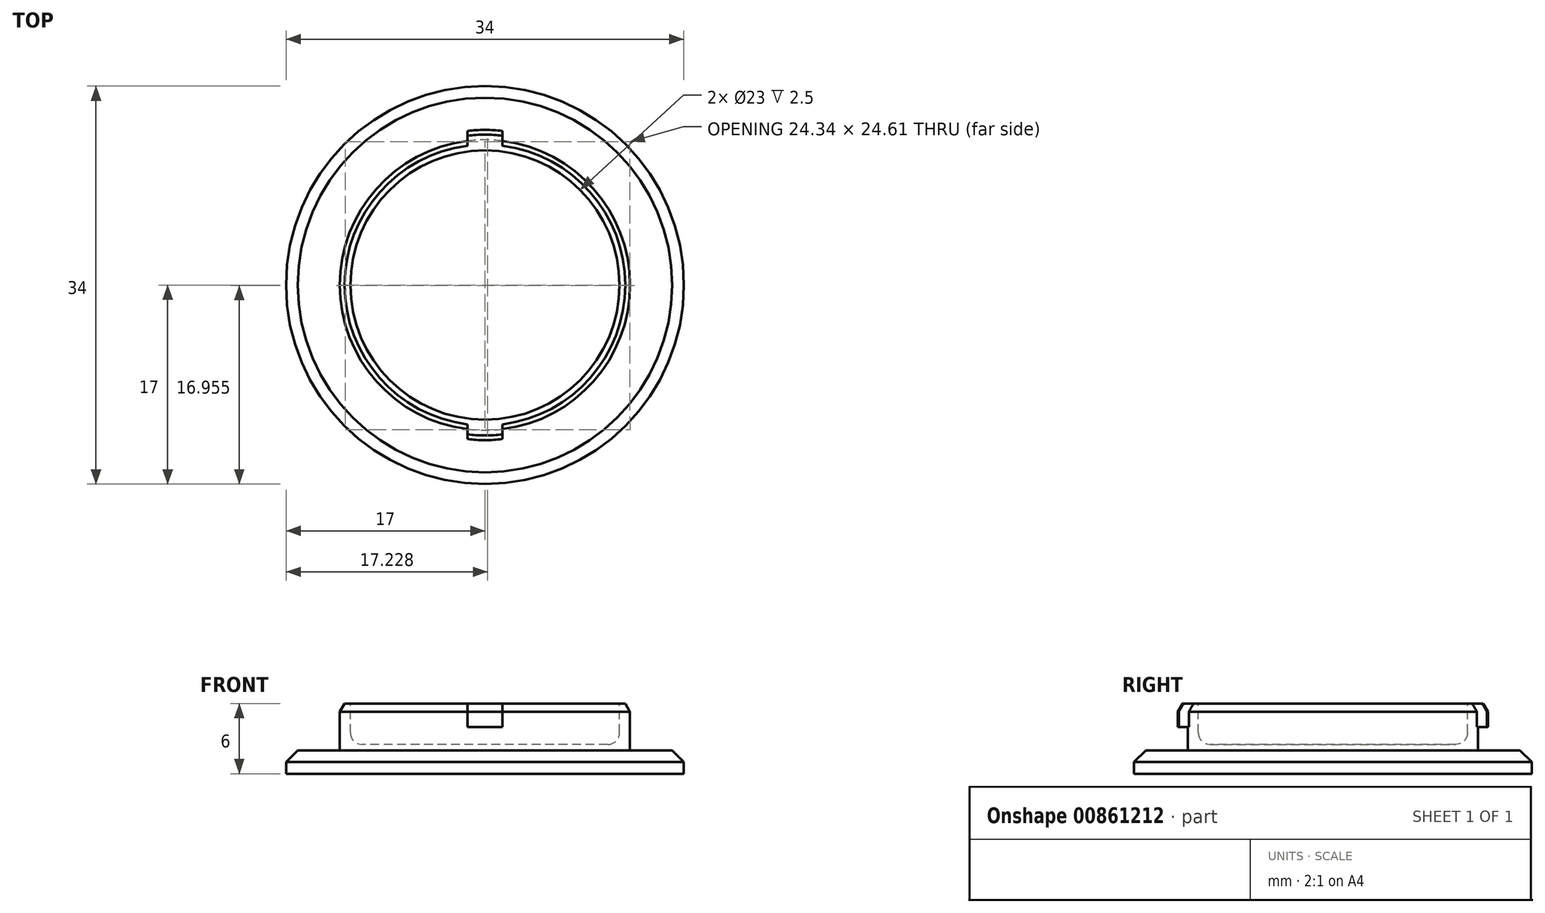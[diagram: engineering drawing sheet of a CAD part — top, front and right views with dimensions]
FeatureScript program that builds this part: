
annotation { "Feature Type Name" : "Feature", "Feature Type Description" : "" }
export const myFeature = defineFeature(function(context is Context, id is Id, definition is map)
    precondition{}
    {
        {
            var Q0;
            Q0=qCreatedBy(makeId("Top.planeOp"),FACE);
            var sketch = newSketch(context, id + "F0", { "sketchPlane" : qUnion([Q0])});
            skCircle(sketch, "E0", {"center": v(0, 0) * mm, "radius": 17 * mm});
            skSolve(sketch);
        }
        {
            var Q0;
            Q0=makeQuery(id+"F0.imprint","IMPRINT",FACE,{"disambiguationData":[TD([[makeQuery(id+"F0.imprint","IMPRINT",EDGE,{"derivedFrom":sQuery(id+"F0.wireOp",EDGE,"E0")}),1.0]])]});
            extrude(context, id + "F1", {"entities" : qUnion([Q0]), "depth" : 2 * mm, "offsetDistance" : 25 * mm});
        }
        {
            var Q0;
            Q0=makeQuery(id+"F1.opExtrude","CAP_FACE",FACE,{"disambiguationData":[OSD([sQuery(id+"F0.wireOp",EDGE,"E0")])],"isStart":false});
            var sketch = newSketch(context, id + "F2", { "sketchPlane" : qUnion([Q0])});
            skCircle(sketch, "E1", {"center": v(0, 0) * mm, "radius": 12.4 * mm});
            skSolve(sketch);
        }
        {
            var Q0;
            Q0=makeQuery(id+"F2.imprint","IMPRINT",FACE,{"disambiguationData":[TD([[makeQuery(id+"F2.imprint","IMPRINT",EDGE,{"derivedFrom":sQuery(id+"F2.wireOp",EDGE,"E1")}),1.0]])]});
            extrude(context, id + "F3", {"entities" : qUnion([Q0]), "operationType" : NewBodyOperationType.ADD, "depth" : 4 * mm, "offsetDistance" : 25 * mm});
        }
        {
            var Q0;
            Q0=makeQuery(id+"F3.opExtrude","CAP_FACE",FACE,{"disambiguationData":[OSD([sQuery(id+"F2.wireOp",EDGE,"E1")])],"isStart":false});
            var sketch = newSketch(context, id + "F4", { "sketchPlane" : qUnion([Q0])});
            skCircle(sketch, "E2", {"center": v(0, 0) * mm, "radius": 11.5 * mm});
            skSolve(sketch);
        }
        {
            var Q0;
            Q0=makeQuery(id+"F4.imprint","IMPRINT",FACE,{"disambiguationData":[TD([[makeQuery(id+"F4.imprint","IMPRINT",EDGE,{"derivedFrom":sQuery(id+"F4.wireOp",EDGE,"E2")}),1.0]])]});
            extrude(context, id + "F5", {"entities" : qUnion([Q0]), "operationType" : NewBodyOperationType.REMOVE, "oppositeDirection" : true, "depth" : 3.5 * mm, "offsetDistance" : 25 * mm});
        }
        {
            var Q0;
            Q0=makeQuery(id+"F3.opExtrude","CAP_FACE",FACE,{"disambiguationData":[OSD([sQuery(id+"F2.wireOp",EDGE,"E1")])],"isStart":false});
            var sketch = newSketch(context, id + "F6", { "sketchPlane" : qUnion([Q0])});
            skArc(sketch, "E3", {"start": v(-1.5, -13.16) * mm, "mid": v(0, -13.25) * mm, "end": v(1.5, -13.16) * mm});
            skLineSegment(sketch, "E4", {"start": v(-1.5, 13.16) * mm, "end": v(-1.5, -13.16) * mm});
            skLineSegment(sketch, "E5", {"start": v(1.5, 13.16) * mm, "end": v(1.5, -13.16) * mm});
            skArc(sketch, "E6.trimOffspring", {"start": v(1.5, 13.16) * mm, "mid": v(0, 13.25) * mm, "end": v(-1.5, 13.16) * mm});
            skSolve(sketch);
        }
        {
            var Q0;
            {var subQ0=sQuery(id+"F6.wireOp",EDGE,"E6.trimOffspring");Q0=makeQuery(id+"F6.imprint","IMPRINT",FACE,{"disambiguationData":[TD([[makeQuery(id+"F6.imprint","IMPRINT",EDGE,{"derivedFrom":subQ0}),1.0]])]});}
            var Q1;
            {var subQ0=sQuery(id+"F6.wireOp",EDGE,"E3");Q1=makeQuery(id+"F6.imprint","IMPRINT",FACE,{"disambiguationData":[TD([[makeQuery(id+"F6.imprint","IMPRINT",EDGE,{"derivedFrom":subQ0}),1.0]])]});}
            extrude(context, id + "F7", {"entities" : qUnion([Q0, Q1]), "operationType" : NewBodyOperationType.ADD, "oppositeDirection" : true, "depth" : 2 * mm, "offsetDistance" : 25 * mm});
        }
        {
            var Q0;
            Q0=makeQuery(id+"F5.boolean.opBoolean","COPY",EDGE,{"derivedFrom":makeQuery(id+"F5.opExtrude","CAP_EDGE",EDGE,{"disambiguationData":[OSD([sQuery(id+"F4.wireOp",EDGE,"E2")])],"isStart":false})});
            var Q1;
            Q1=makeQuery(id+"F3.opExtrude","CAP_EDGE",EDGE,{"disambiguationData":[OSD([sQuery(id+"F2.wireOp",EDGE,"E1")])],"isStart":true});
            fillet(context, id + "F8", {"entities" : qUnion([Q0, Q1]), "radius" : 1 * mm, "tangentPropagation" : true, "allowEdgeOverflow" : false});
        }
        {
            var Q0;
            Q0=makeQuery(id+"F1.opExtrude","CAP_EDGE",EDGE,{"disambiguationData":[OSD([sQuery(id+"F0.wireOp",EDGE,"E0")])],"isStart":false});
            chamfer(context, id + "F9", {"entities" : qUnion([Q0]), "width" : 1 * mm, "tangentPropagation" : true});
        }
        {
            var Q0;
            {var subQ0=sQuery(id+"F6.wireOp",EDGE,"E6.trimOffspring");var subQ1=sQuery(id+"F6.wireOp",EDGE,"E4");var subQ2=sQuery(id+"F2.wireOp",EDGE,"E1");var subQ3=makeQuery(id+"F3.opExtrude","CAP_EDGE",EDGE,{"disambiguationData":[OSD([subQ2])],"isStart":false});Q0=makeQuery(id+"F7.boolean.opBoolean","SPLIT",EDGE,{"disambiguationData":[TD([makeQuery(id+"F7.opExtrude","SWEPT_FACE",FACE,{"disambiguationData":[OSD([subQ1]),TDD([makeQuery(id+"F6.imprint","IMPRINT",EDGE,{"disambiguationData":[TD([[makeQuery(id+"F6.imprint","INTERSECT",VERTEX,{"derivedFrom":[subQ1,subQ0]}),-1.0]])],"derivedFrom":subQ1})])]})])],"derivedFrom":subQ3});}
            var Q1;
            {var subQ0=sQuery(id+"F6.wireOp",EDGE,"E5");var subQ3=sQuery(id+"F2.wireOp",EDGE,"E1");var subQ4=sQuery(id+"F6.wireOp",EDGE,"E6.trimOffspring");var subQ5=makeQuery(id+"F3.opExtrude","CAP_EDGE",EDGE,{"disambiguationData":[OSD([subQ3])],"isStart":false});Q1=makeQuery(id+"F7.boolean.opBoolean","SPLIT",EDGE,{"disambiguationData":[TD([makeQuery(id+"F7.opExtrude","SWEPT_FACE",FACE,{"disambiguationData":[OSD([subQ0]),TDD([makeQuery(id+"F6.imprint","IMPRINT",EDGE,{"disambiguationData":[TD([[makeQuery(id+"F6.imprint","INTERSECT",VERTEX,{"derivedFrom":[subQ0,subQ4]}),-1.0]])],"derivedFrom":subQ0})])]})])],"derivedFrom":subQ5});}
            var Q2;
            Q2=makeQuery(id+"F7.opExtrude","CAP_EDGE",EDGE,{"disambiguationData":[OSD([sQuery(id+"F6.wireOp",EDGE,"E3")])],"isStart":true});
            var Q3;
            Q3=makeQuery(id+"F7.opExtrude","CAP_EDGE",EDGE,{"disambiguationData":[OSD([sQuery(id+"F6.wireOp",EDGE,"E6.trimOffspring")])],"isStart":true});
            chamfer(context, id + "F10", {"entities" : qUnion([Q0, Q1, Q2, Q3]), "chamferType" : ChamferType.OFFSET_ANGLE, "width" : 0.7 * mm, "oppositeDirection" : true, "angle" : 30 * degree, "tangentPropagation" : true});
        }
        {
            var Q0;
            Q0=makeQuery(id+"F1.opExtrude","SWEPT_BODY",BODY,{"disambiguationData":[OSD([sQuery(id+"F0.wireOp",EDGE,"E0")])]});
            transform(context, id + "F11", {"entities" : qUnion([Q0]), "transformType" : TransformType.TRANSLATION_3D, "dx" : 0 * mm, "dy" : 0 * mm, "dz" : 0 * mm, "makeCopy" : true});
        }
    });
